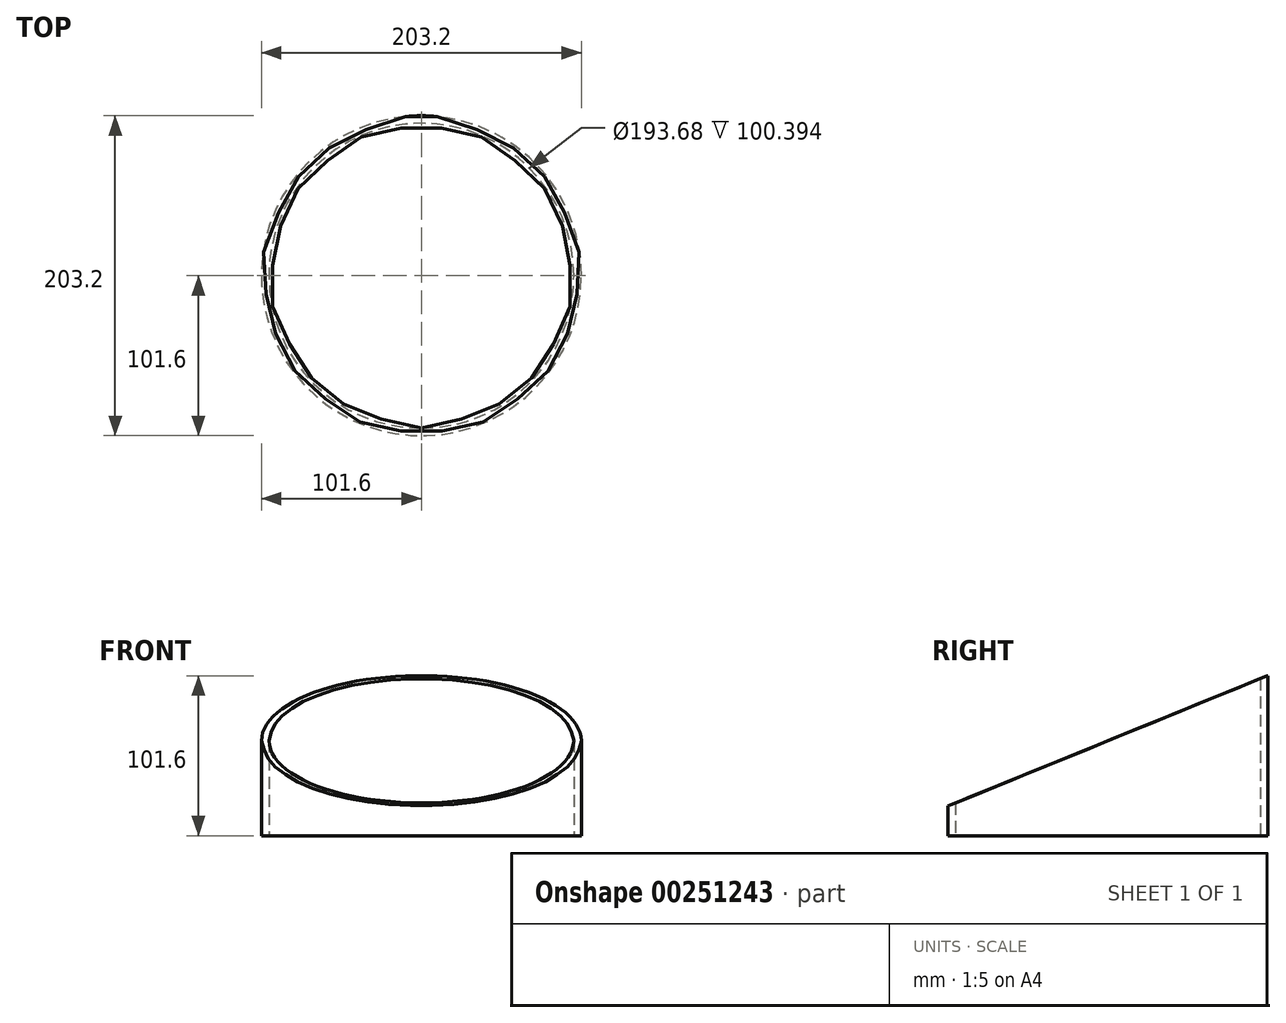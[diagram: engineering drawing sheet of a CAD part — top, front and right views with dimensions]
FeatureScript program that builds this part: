
annotation { "Feature Type Name" : "Feature", "Feature Type Description" : "" }
export const myFeature = defineFeature(function(context is Context, id is Id, definition is map)
    precondition{}
    {
        {
            var Q0;
            Q0=qCreatedBy(makeId("Top.planeOp"),FACE);
            var sketch = newSketch(context, id + "F0", { "sketchPlane" : qUnion([Q0])});
            skCircle(sketch, "E0", {"center": v(0, 0) * mm, "radius": 101.6 * mm});
            skCircle(sketch, "E1", {"center": v(0, 0) * mm, "radius": 96.84 * mm});
            skSolve(sketch);
        }
        {
            var Q0;
            Q0 = qSketchRegion(id + "F0", true);
            extrude(context, id + "F1", {"entities" : qUnion([Q0]), "depth" : 101.6 * mm});
        }
        {
            var Q0;
            Q0=qCreatedBy(makeId("Right.planeOp"),FACE);
            var sketch = newSketch(context, id + "F2", { "sketchPlane" : qUnion([Q0])});
            skLineSegment(sketch, "E2", {"start": v(101.12, 101.6) * mm, "end": v(-119.42, 101.6) * mm});
            skLineSegment(sketch, "E3", {"start": v(-119.42, 101.6) * mm, "end": v(-119.42, 11.6) * mm});
            skLineSegment(sketch, "E4", {"start": v(-119.42, 11.6) * mm, "end": v(101.12, 101.6) * mm});
            skSolve(sketch);
        }
        {
            var Q0;
            Q0 = qSketchRegion(id + "F2", true);
            extrude(context, id + "F3", {"entities" : qUnion([Q0]), "operationType" : NewBodyOperationType.REMOVE, "endBound" : BoundingType.THROUGH_ALL, "oppositeDirection" : true, "depth" : 25.4 * mm, "hasSecondDirection" : true, "secondDirectionBound" : SecondDirectionBoundingType.THROUGH_ALL, "secondDirectionOppositeDirection" : false, "secondDirectionDepth" : 25.4 * mm});
        }
    });
